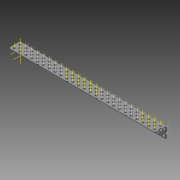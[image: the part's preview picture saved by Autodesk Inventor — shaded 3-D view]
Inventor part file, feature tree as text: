
AUTODESK INVENTOR PART (.ipt)
format: ipt  version: 2015 (Build 190159000, 159)  size: 2,392,064 bytes
history: native  units: in
note: dims shown in document units (in); Inventor stores cm internally (conversion verified against a paired STEP export)
features: other x155, pattern_linear x4, sheet_metal_op x1, extrude x1, imported_body x1, sketch x1
ambient origin geometry x8: Origin, YZ Plane, XZ Plane, XY Plane, X Axis, Y Axis, Z Axis, Center Point
bodies: Body1 (feature_tree)
feature tree (163):
  sheet_metal_op  "Fold1"
  other  "L-Channel"
  extrude  "length cut"  Depth=0.5in
  other  "top out axis"
  other  "top inner axis"
  other  "back out axis"
  other  "back inner axis"
  pattern_linear  "top outer axes"  Count1=2 Spacing1=0.5in
  pattern_linear  "top inner axes"  Spacing1=0.5in  [1 undecoded]
  pattern_linear  "back outer axes"  Count1=2 Spacing1=0.5in
  pattern_linear  "back inner axes"  Spacing1=0.5in  [1 undecoded]
  other  "right plane"
  imported_body  "Base1"
  sketch  "Sketch1"  dims[d1=0.0in d4=0.5in d5=0.7874in d7=0.5in d10=0.5in d13=0.5in d14=0.7874in d16=0.5in d19=0.5in d20=-12.5in d21=0.0in d22=0.0in d23=0.0in d24=0.0in d25=0.0in d26=0.0in]
  other  "Work Point1"
  other  "Work Point2"
  other  "Work Point3"
  other  "Work Point4"
  other  "Work Axis5"
  other  "Work Axis6"
  other  "Work Axis7"
  other  "Work Axis8"
  other  "Work Axis11"
  other  "Work Axis12"
  other  "Work Axis13"
  other  "Work Axis14"
  other  "Work Axis15"
  other  "Work Axis18"
  other  "Work Axis19"
  other  "Work Axis20"
  other  "Work Axis23"
  other  "Work Axis24"
  other  "Work Axis25"
  other  "Work Axis26"
  other  "Work Axis29"
  other  "Work Axis30"
  other  "Work Axis31"
  other  "Work Axis32"
  other  "Work Axis33"
  other  "Work Axis36"
  other  "Work Axis37"
  other  "Work Axis38"
  other  "Work Axis41"
  other  "Work Axis42"
  other  "Work Axis43"
  other  "Work Axis44"
  other  "Work Axis45"
  other  "Work Axis46"
  other  "Work Axis47"
  other  "Work Axis48"
  other  "Work Axis49"
  other  "Work Axis50"
  other  "Work Axis51"
  other  "Work Axis52"
  other  "Work Axis53"
  other  "Work Axis54"
  other  "Work Axis55"
  other  "Work Axis56"
  other  "Work Axis57"
  other  "Work Axis58"
  other  "Work Axis59"
  other  "Work Axis60"
  other  "Work Axis61"
  other  "Work Axis62"
  other  "Work Axis63"
  other  "Work Axis64"
  other  "Work Axis65"
  other  "Work Axis66"
  other  "Work Axis67"
  other  "Work Axis68"
  other  "Work Axis69"
  other  "Work Axis70"
  other  "Work Axis71"
  other  "Work Axis72"
  other  "Work Axis73"
  other  "Work Axis74"
  other  "Work Axis75"
  other  "Work Axis76"
  other  "Work Axis77"
  other  "Work Axis78"
  other  "Work Axis79"
  other  "Work Axis80"
  other  "Work Axis81"
  other  "Work Axis82"
  other  "Work Axis83"
  other  "Work Axis84"
  other  "Work Axis85"
  other  "Work Axis86"
  other  "Work Axis87"
  other  "Work Axis88"
  other  "Work Axis89"
  other  "Work Axis90"
  other  "Work Axis91"
  other  "Work Axis92"
  other  "Work Axis93"
  other  "Work Axis94"
  other  "Work Axis95"
  other  "Work Axis96"
  other  "Work Axis97"
  other  "Work Axis98"
  other  "Work Axis99"
  other  "Work Axis100"
  other  "Work Axis101"
  other  "Work Axis102"
  other  "Work Axis103"
  other  "Work Axis104"
  other  "Work Axis105"
  other  "Work Axis106"
  other  "Work Axis107"
  other  "Work Axis108"
  other  "Work Axis109"
  other  "Work Axis110"
  other  "Work Axis111"
  other  "Work Axis112"
  other  "Work Axis113"
  other  "Work Axis114"
  other  "Work Axis115"
  other  "Work Axis116"
  other  "Work Axis117"
  other  "Work Axis118"
  other  "Work Axis119"
  other  "Work Axis120"
  other  "Work Axis121"
  other  "Work Axis122"
  other  "Work Axis123"
  other  "Work Axis124"
  other  "Work Axis125"
  other  "Work Axis126"
  other  "Work Axis127"
  other  "Work Axis128"
  other  "Work Axis129"
  other  "Work Axis130"
  other  "Work Axis131"
  other  "Work Axis132"
  other  "Work Axis133"
  other  "Work Axis134"
  other  "Work Axis135"
  other  "Work Axis136"
  other  "Work Axis137"
  other  "Work Axis138"
  other  "Work Axis139"
  other  "Work Axis140"
  other  "Work Axis141"
  other  "Work Axis142"
  other  "Work Axis143"
  other  "Work Axis144"
  other  "Work Axis145"
  other  "Work Axis146"
  other  "Work Axis147"
  other  "Work Axis148"
  other  "Work Axis149"
  other  "Work Axis150"
  other  "Work Axis151"
  other  "Work Axis152"
  other  "Work Axis153"
  other  "Work Axis154"
  other  "Work Axis155"
  other  "Work Axis156"
  other  "Work Axis157"
  other  "Work Axis158"
  other  "Work Axis159"
  other  "Work Axis160"
  other  "left plane"
note: 2 required parameter values undecoded (feature->parameter linkage not recoverable at this tier; creation-order binding heuristic only, values carry confidence <= 0.55)
